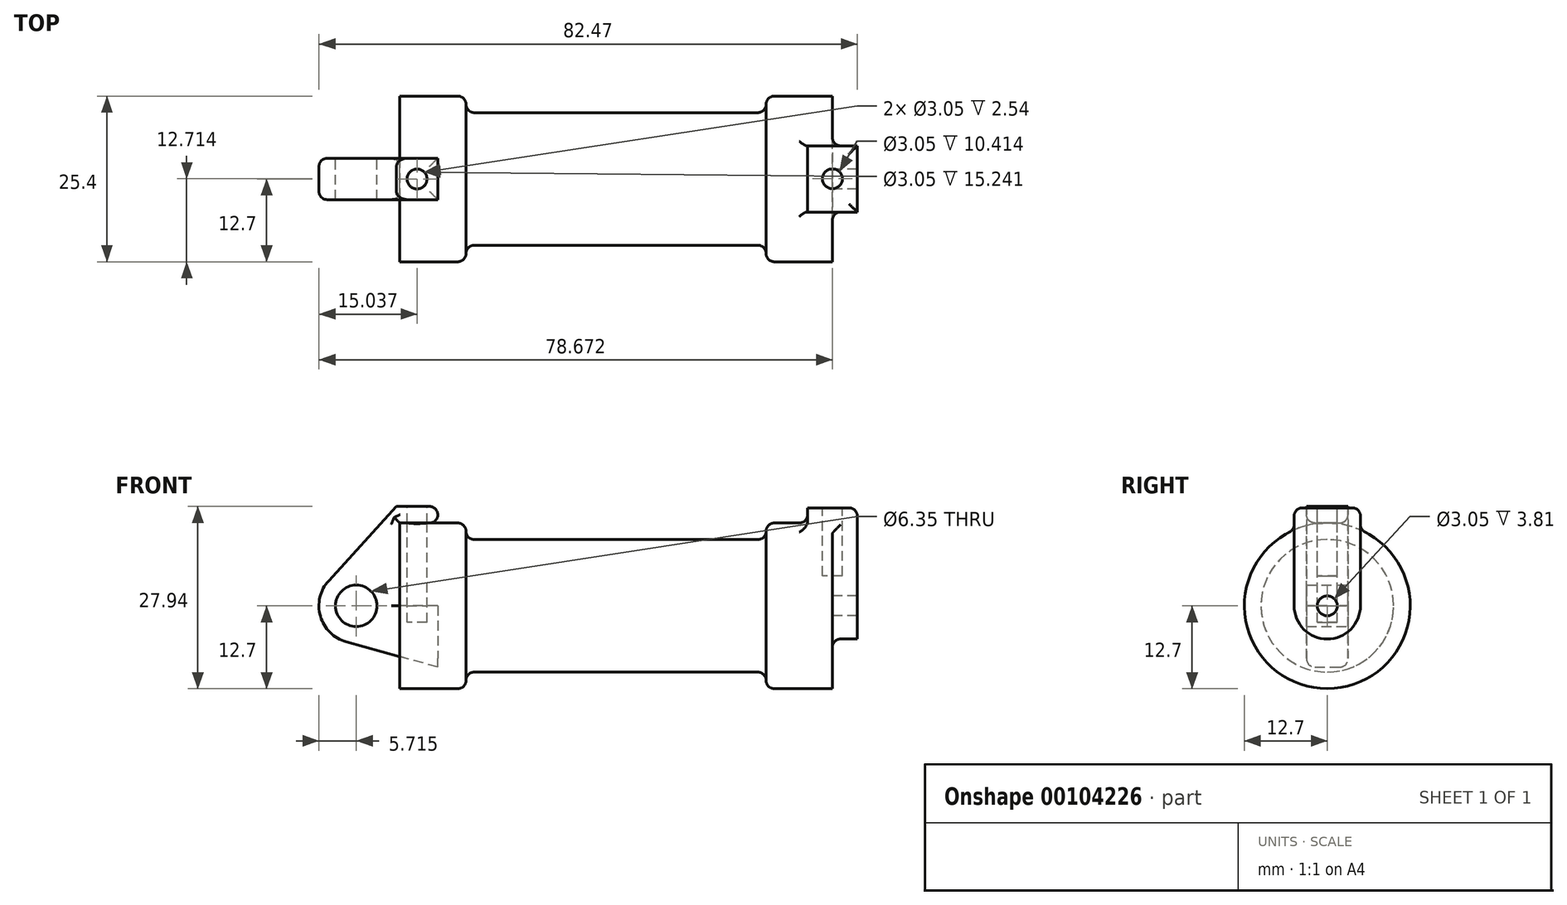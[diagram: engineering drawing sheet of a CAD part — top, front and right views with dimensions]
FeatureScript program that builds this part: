
annotation { "Feature Type Name" : "Feature", "Feature Type Description" : "" }
export const myFeature = defineFeature(function(context is Context, id is Id, definition is map)
    precondition{}
    {
        {
            var Q0;
            Q0=qCreatedBy(makeId("Front.planeOp"),FACE);
            var sketch = newSketch(context, id + "F0", { "sketchPlane" : qUnion([Q0])});
            skLineSegment(sketch, "E0", {"start": v(0, 0) * mm, "end": v(0, 12.7) * mm});
            skLineSegment(sketch, "E1", {"start": v(0, 12.7) * mm, "end": v(10.16, 12.7) * mm});
            skLineSegment(sketch, "E2", {"start": v(10.16, 12.7) * mm, "end": v(10.16, 10.16) * mm});
            skLineSegment(sketch, "E3", {"start": v(10.16, 10.16) * mm, "end": v(56.13, 10.16) * mm});
            skLineSegment(sketch, "E4", {"start": v(56.13, 10.16) * mm, "end": v(56.13, 12.7) * mm});
            skLineSegment(sketch, "E5", {"start": v(56.13, 12.7) * mm, "end": v(66.3, 12.7) * mm});
            skLineSegment(sketch, "E6", {"start": v(66.3, 12.7) * mm, "end": v(66.3, 0) * mm});
            skLineSegment(sketch, "E7", {"start": v(66.3, 0) * mm, "end": v(0, 0) * mm});
            skLineSegment(sketch, "E8", {"start": v(5.84, 15.24) * mm, "end": v(-0.5, 15.24) * mm});
            skLineSegment(sketch, "E9", {"start": v(-0.5, 15.24) * mm, "end": v(-10.88, 3.85) * mm});
            skLineSegment(sketch, "E10", {"start": v(0, 0) * mm, "end": v(-6.65, 0) * mm});
            skCircle(sketch, "E11", {"center": v(-6.65, 0) * mm, "radius": 5.72 * mm});
            skCircle(sketch, "E12", {"center": v(-6.65, 0) * mm, "radius": 3.18 * mm});
            skLineSegment(sketch, "E13", {"start": v(5.84, 15.24) * mm, "end": v(5.84, -9.4) * mm});
            skLineSegment(sketch, "E14", {"start": v(5.84, -9.4) * mm, "end": v(-8.18, -5.5) * mm});
            skSolve(sketch);
        }
        {
            var Q0;
            {var subQ4=sQuery(id+"F0.wireOp",EDGE,"E12");Q0=makeQuery(id+"F0.imprint","IMPRINT",FACE,{"disambiguationData":[TD([[makeQuery(id+"F0.imprint","IMPRINT",EDGE,{"derivedFrom":subQ4}),-1.0]])]});}
            var Q1;
            {var subQ3=sQuery(id+"F0.wireOp",EDGE,"E0");Q1=makeQuery(id+"F0.imprint","IMPRINT",FACE,{"disambiguationData":[TD([[makeQuery(id+"F0.imprint","IMPRINT",EDGE,{"derivedFrom":subQ3}),1.0]])]});}
            var Q2;
            {var subQ0=sQuery(id+"F0.wireOp",EDGE,"E14");Q2=makeQuery(id+"F0.imprint","IMPRINT",FACE,{"disambiguationData":[TD([[makeQuery(id+"F0.imprint","IMPRINT",EDGE,{"derivedFrom":subQ0}),-1.0]])]});}
            extrude(context, id + "F1", {"entities" : qUnion([Q0, Q1, Q2]), "endBound" : BoundingType.SYMMETRIC, "depth" : 6.35 * mm});
        }
        {
            var Q0;
            {var subQ0=sQuery(id+"F0.wireOp",EDGE,"E0");Q0=makeQuery(id+"F0.imprint","IMPRINT",FACE,{"disambiguationData":[TD([[makeQuery(id+"F0.imprint","IMPRINT",EDGE,{"derivedFrom":subQ0}),-1.0]])]});}
            var Q1;
            {var subQ0=sQuery(id+"F0.wireOp",EDGE,"E2");Q1=makeQuery(id+"F0.imprint","IMPRINT",FACE,{"disambiguationData":[TD([[makeQuery(id+"F0.imprint","IMPRINT",EDGE,{"derivedFrom":subQ0}),-1.0]])]});}
            var Q2;
            Q2=sQuery(id+"F0.wireOp",EDGE,"E7");
            revolve(context, id + "F2", {"entities" : qUnion([Q0, Q1]), "axis" : qUnion([Q2]), "revolveType" : RevolveType.FULL});
        }
        {
            var Q0;
            Q0=makeQuery(id+"F2.opRevolve","SWEPT_FACE",FACE,{"disambiguationData":[OSD([sQuery(id+"F0.wireOp",EDGE,"E6")])]});
            var sketch = newSketch(context, id + "F3", { "sketchPlane" : qUnion([Q0])});
            skCircle(sketch, "E15", {"center": v(0, 0) * mm, "radius": 1.52 * mm});
            skCircle(sketch, "E16", {"center": v(0, 0) * mm, "radius": 5.08 * mm});
            skLineSegment(sketch, "E17", {"start": v(-5.08, 0) * mm, "end": v(-5.08, 15.03) * mm});
            skLineSegment(sketch, "E18", {"start": v(5.08, 0) * mm, "end": v(5.08, 15.03) * mm});
            skLineSegment(sketch, "E19", {"start": v(5.08, 15.03) * mm, "end": v(-5.08, 15.03) * mm});
            skSolve(sketch);
        }
        {
            var Q0;
            {var subQ0=sQuery(id+"F3.wireOp",EDGE,"E17");var subQ1=sQuery(id+"F3.wireOp",EDGE,"E16");var subQ2=makeQuery(id+"F3.imprint","INTERSECT",VERTEX,{"derivedFrom":[subQ1,subQ0]});Q0=makeQuery(id+"F3.imprint","IMPRINT",FACE,{"disambiguationData":[TD([[makeQuery(id+"F3.imprint","IMPRINT",EDGE,{"disambiguationData":[TD([[subQ2,1.0]])],"derivedFrom":subQ1}),-1.0]])]});}
            var Q1;
            Q1=makeQuery(id+"F3.imprint","IMPRINT",FACE,{"disambiguationData":[TD([[makeQuery(id+"F3.imprint","IMPRINT",EDGE,{"derivedFrom":sQuery(id+"F3.wireOp",EDGE,"E15")}),-1.0]])]});
            var Q2;
            {var subQ0=sQuery(id+"F3.wireOp",EDGE,"E19");Q2=makeQuery(id+"F3.imprint","IMPRINT",FACE,{"disambiguationData":[TD([[makeQuery(id+"F3.imprint","IMPRINT",EDGE,{"derivedFrom":subQ0}),1.0]])]});}
            extrude(context, id + "F4", {"entities" : qUnion([Q0, Q1, Q2]), "operationType" : NewBodyOperationType.ADD, "endBound" : BoundingType.SYMMETRIC, "depth" : 7.62 * mm});
        }
        {
            var Q0;
            Q0=makeQuery(id+"F4.opExtrude","SWEPT_FACE",FACE,{"disambiguationData":[OSD([sQuery(id+"F3.wireOp",EDGE,"E19")])]});
            var sketch = newSketch(context, id + "F5", { "sketchPlane" : qUnion([Q0])});
            skCircle(sketch, "E20", {"center": v(66.3, 0.01) * mm, "radius": 1.52 * mm});
            skSolve(sketch);
        }
        {
            var Q0;
            Q0=makeQuery(id+"F5.imprint","IMPRINT",FACE,{"disambiguationData":[TD([[makeQuery(id+"F5.imprint","IMPRINT",EDGE,{"derivedFrom":sQuery(id+"F5.wireOp",EDGE,"E20")}),1.0]])]});
            var Q1;
            Q1=sQuery(id+"F5.wireOp",EDGE,"E20");
            extrude(context, id + "F6", {"entities" : qUnion([Q0]), "operationType" : NewBodyOperationType.REMOVE, "surfaceEntities" : qUnion([Q1]), "oppositeDirection" : true, "depth" : 10.4 * mm});
        }
        {
            var Q0;
            Q0=makeQuery(id+"F1.opExtrude","SWEPT_FACE",FACE,{"disambiguationData":[OSD([sQuery(id+"F0.wireOp",EDGE,"E8")])]});
            var sketch = newSketch(context, id + "F7", { "sketchPlane" : qUnion([Q0])});
            skLineSegment(sketch, "E21", {"start": v(2.67, 3.18) * mm, "end": v(2.67, -3.18) * mm, "construction": true});
            skLineSegment(sketch, "E22", {"start": v(-0.5, 0) * mm, "end": v(5.84, 0) * mm, "construction": true});
            skCircle(sketch, "E23", {"center": v(2.67, 0) * mm, "radius": 1.53 * mm});
            skSolve(sketch);
        }
        {
            var Q0;
            Q0=makeQuery(id+"F7.imprint","IMPRINT",FACE,{"disambiguationData":[TD([[makeQuery(id+"F7.imprint","IMPRINT",EDGE,{"derivedFrom":sQuery(id+"F7.wireOp",EDGE,"E23")}),1.0]])]});
            var Q1;
            Q1=sQuery(id+"F7.wireOp",EDGE,"E23");
            extrude(context, id + "F8", {"entities" : qUnion([Q0]), "operationType" : NewBodyOperationType.REMOVE, "surfaceEntities" : qUnion([Q1]), "oppositeDirection" : true, "depth" : 17.78 * mm});
        }
        {
            var Q0;
            Q0=makeQuery(id+"F2.opRevolve","SWEPT_FACE",FACE,{"disambiguationData":[OSD([sQuery(id+"F0.wireOp",EDGE,"E4")])]});
            var Q1;
            Q1=makeQuery(id+"F2.opRevolve","SWEPT_FACE",FACE,{"disambiguationData":[OSD([sQuery(id+"F0.wireOp",EDGE,"E3")])]});
            fillet(context, id + "F9", {"entities" : qUnion([Q0, Q1]), "radius" : 1.27 * mm, "tangentPropagation" : true, "allowEdgeOverflow" : false});
        }
        {
            var Q0;
            Q0=makeQuery(id+"F2.opRevolve","SWEPT_FACE",FACE,{"disambiguationData":[OSD([sQuery(id+"F0.wireOp",EDGE,"E2")])]});
            var Q1;
            Q1=makeQuery(id+"F9.opFillet","BLEND_FACE",FACE,{"disambiguationData":[OSD([sQuery(id+"F0.wireOp",EDGE,"E2"),sQuery(id+"F0.wireOp",EDGE,"E3")])]});
            fillet(context, id + "F10", {"entities" : qUnion([Q0, Q1]), "radius" : 1.27 * mm, "tangentPropagation" : true, "allowEdgeOverflow" : false});
        }
        {
            var Q0;
            Q0=makeQuery(id+"F1.opExtrude","CAP_EDGE",EDGE,{"disambiguationData":[OSD([sQuery(id+"F0.wireOp",EDGE,"E0")])],"isStart":false});
            var Q1;
            Q1=makeQuery(id+"F1.opExtrude","CAP_EDGE",EDGE,{"disambiguationData":[OSD([sQuery(id+"F0.wireOp",EDGE,"E0")])],"isStart":true});
            var Q2;
            Q2=makeQuery(id+"F1.opExtrude","CAP_EDGE",EDGE,{"disambiguationData":[OSD([sQuery(id+"F0.wireOp",EDGE,"E9")])],"isStart":false});
            var Q3;
            Q3=makeQuery(id+"F1.opExtrude","CAP_EDGE",EDGE,{"disambiguationData":[OSD([sQuery(id+"F0.wireOp",EDGE,"E9")])],"isStart":true});
            var Q4;
            Q4=makeQuery(id+"F1.opExtrude","SWEPT_EDGE",EDGE,{"disambiguationData":[OSD([sQuery(id+"F0.wireOp",EDGE,"E8"),sQuery(id+"F0.wireOp",EDGE,"E13")])]});
            var Q5;
            Q5=makeQuery(id+"F1.opExtrude","CAP_EDGE",EDGE,{"disambiguationData":[OSD([sQuery(id+"F0.wireOp",EDGE,"E1")])],"isStart":false});
            var Q6;
            Q6=makeQuery(id+"F1.opExtrude","CAP_EDGE",EDGE,{"disambiguationData":[OSD([sQuery(id+"F0.wireOp",EDGE,"E1")])],"isStart":true});
            var Q7;
            Q7=makeQuery(id+"F1.opExtrude","SWEPT_EDGE",EDGE,{"disambiguationData":[OSD([sQuery(id+"F0.wireOp",EDGE,"E1"),sQuery(id+"F0.wireOp",EDGE,"E13")])]});
            var Q8;
            Q8=makeQuery(id+"F1.opExtrude","CAP_EDGE",EDGE,{"disambiguationData":[OSD([sQuery(id+"F0.wireOp",EDGE,"E11")])],"isStart":false});
            var Q9;
            Q9=makeQuery(id+"F1.opExtrude","CAP_EDGE",EDGE,{"disambiguationData":[OSD([sQuery(id+"F0.wireOp",EDGE,"E14")])],"isStart":false});
            var Q10;
            Q10=makeQuery(id+"F1.opExtrude","CAP_EDGE",EDGE,{"disambiguationData":[OSD([sQuery(id+"F0.wireOp",EDGE,"E14")])],"isStart":true});
            var Q11;
            Q11=makeQuery(id+"F1.opExtrude","CAP_EDGE",EDGE,{"disambiguationData":[OSD([sQuery(id+"F0.wireOp",EDGE,"E11")])],"isStart":true});
            fillet(context, id + "F11", {"entities" : qUnion([Q0, Q1, Q2, Q3, Q4, Q5, Q6, Q7, Q8, Q9, Q10, Q11]), "radius" : 1.27 * mm, "tangentPropagation" : true, "allowEdgeOverflow" : false});
        }
        {
            var Q0;
            Q0=makeQuery(id+"F4.boolean.opBoolean","INTERSECT",EDGE,{"derivedFrom":[makeQuery(id+"F2.opRevolve","SWEPT_FACE",FACE,{"disambiguationData":[OSD([sQuery(id+"F0.wireOp",EDGE,"E6")])]}),makeQuery(id+"F4.opExtrude","SWEPT_FACE",FACE,{"disambiguationData":[OSD([sQuery(id+"F3.wireOp",EDGE,"E18")])]})]});
            var Q1;
            Q1=makeQuery(id+"F4.boolean.opBoolean","INTERSECT",EDGE,{"derivedFrom":[makeQuery(id+"F2.opRevolve","SWEPT_FACE",FACE,{"disambiguationData":[OSD([sQuery(id+"F0.wireOp",EDGE,"E6")])]}),makeQuery(id+"F4.opExtrude","SWEPT_FACE",FACE,{"disambiguationData":[OSD([sQuery(id+"F3.wireOp",EDGE,"E17")])]})]});
            var Q2;
            Q2=makeQuery(id+"F4.boolean.opBoolean","INTERSECT",EDGE,{"derivedFrom":[makeQuery(id+"F2.opRevolve","SWEPT_FACE",FACE,{"disambiguationData":[OSD([sQuery(id+"F0.wireOp",EDGE,"E6")])]}),makeQuery(id+"F4.opExtrude","SWEPT_FACE",FACE,{"disambiguationData":[OSD([sQuery(id+"F3.wireOp",EDGE,"E16")])]})]});
            var Q3;
            Q3=makeQuery(id+"F4.boolean.opBoolean","INTERSECT",EDGE,{"derivedFrom":[makeQuery(id+"F2.opRevolve","SWEPT_FACE",FACE,{"disambiguationData":[OSD([sQuery(id+"F0.wireOp",EDGE,"E5")])]}),makeQuery(id+"F4.opExtrude","CAP_FACE",FACE,{"disambiguationData":[OSD([sQuery(id+"F3.wireOp",EDGE,"E15"),sQuery(id+"F3.wireOp",EDGE,"E16"),sQuery(id+"F3.wireOp",EDGE,"E17"),sQuery(id+"F3.wireOp",EDGE,"E18"),sQuery(id+"F3.wireOp",EDGE,"E19")])],"isStart":true})]});
            var Q4;
            Q4=makeQuery(id+"F4.boolean.opBoolean","INTERSECT",EDGE,{"derivedFrom":[makeQuery(id+"F2.opRevolve","SWEPT_FACE",FACE,{"disambiguationData":[OSD([sQuery(id+"F0.wireOp",EDGE,"E5")])]}),makeQuery(id+"F4.opExtrude","SWEPT_FACE",FACE,{"disambiguationData":[OSD([sQuery(id+"F3.wireOp",EDGE,"E18")])]})]});
            var Q5;
            Q5=makeQuery(id+"F4.boolean.opBoolean","INTERSECT",EDGE,{"derivedFrom":[makeQuery(id+"F2.opRevolve","SWEPT_FACE",FACE,{"disambiguationData":[OSD([sQuery(id+"F0.wireOp",EDGE,"E5")])]}),makeQuery(id+"F4.opExtrude","SWEPT_FACE",FACE,{"disambiguationData":[OSD([sQuery(id+"F3.wireOp",EDGE,"E17")])]})]});
            var Q6;
            Q6=makeQuery(id+"F4.opExtrude","SWEPT_EDGE",EDGE,{"disambiguationData":[OSD([sQuery(id+"F3.wireOp",EDGE,"E18"),sQuery(id+"F3.wireOp",EDGE,"E19")])]});
            var Q7;
            Q7=makeQuery(id+"F4.opExtrude","CAP_EDGE",EDGE,{"disambiguationData":[OSD([sQuery(id+"F3.wireOp",EDGE,"E19")])],"isStart":false});
            var Q8;
            Q8=makeQuery(id+"F4.opExtrude","SWEPT_EDGE",EDGE,{"disambiguationData":[OSD([sQuery(id+"F3.wireOp",EDGE,"E17"),sQuery(id+"F3.wireOp",EDGE,"E19")])]});
            fillet(context, id + "F12", {"entities" : qUnion([Q0, Q1, Q2, Q3, Q4, Q5, Q6, Q7, Q8]), "radius" : 1.27 * mm, "tangentPropagation" : true, "allowEdgeOverflow" : false});
        }
    });
